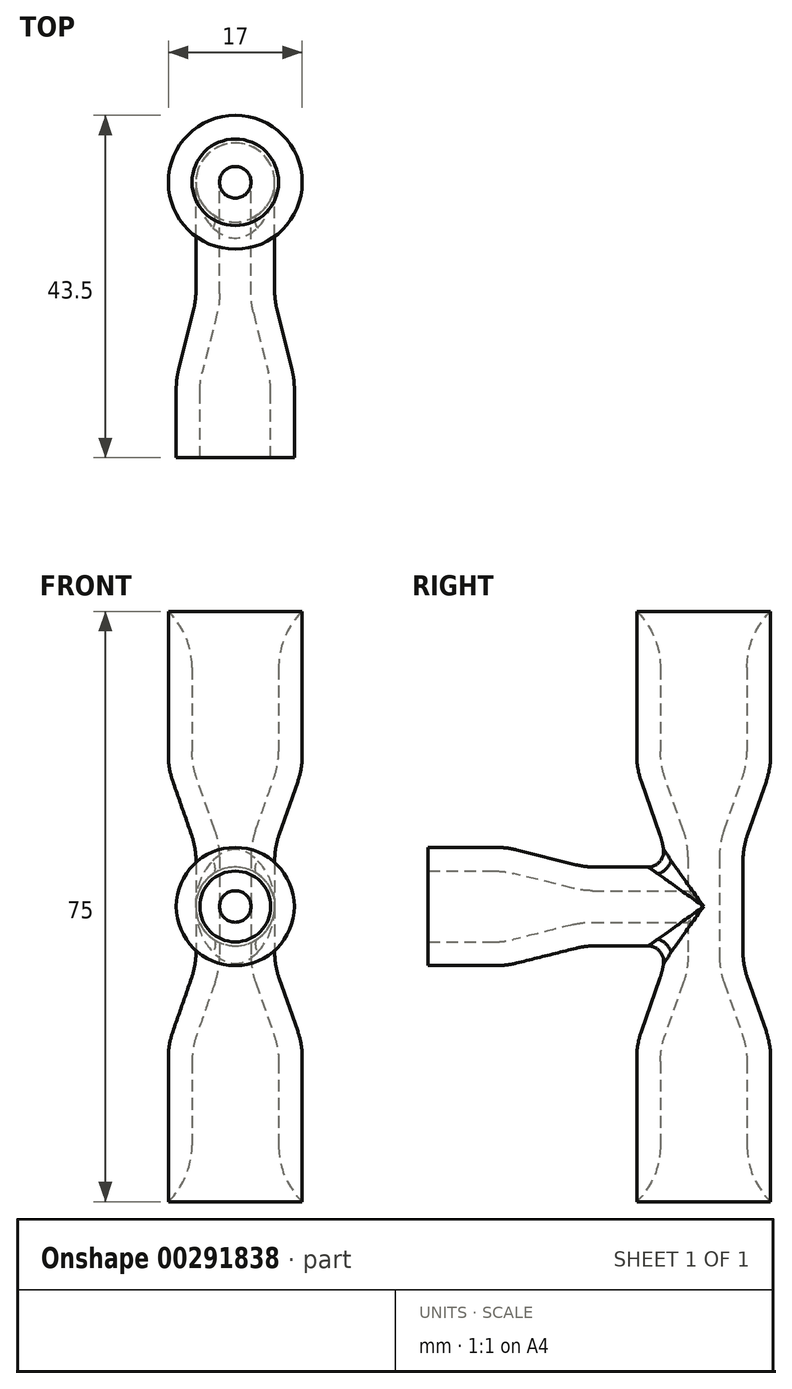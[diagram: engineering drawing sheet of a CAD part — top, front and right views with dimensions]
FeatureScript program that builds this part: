
annotation { "Feature Type Name" : "Feature", "Feature Type Description" : "" }
export const myFeature = defineFeature(function(context is Context, id is Id, definition is map)
    precondition{}
    {
        {
            var Q0;
            Q0=qCreatedBy(makeId("Top.planeOp"),FACE);
            var sketch = newSketch(context, id + "F0", { "sketchPlane" : qUnion([Q0])});
            skCircle(sketch, "E0", {"center": v(0, 0) * mm, "radius": 8.5 * mm});
            skSolve(sketch);
        }
        {
            var Q0;
            Q0=makeQuery(id+"F0.imprint","IMPRINT",FACE,{"disambiguationData":[TD([[makeQuery(id+"F0.imprint","IMPRINT",EDGE,{"derivedFrom":sQuery(id+"F0.wireOp",EDGE,"E0")}),1.0]])]});
            extrude(context, id + "F1", {"entities" : qUnion([Q0]), "depth" : 20 * mm});
        }
        {
            var Q0;
            Q0=makeQuery(id+"F1.opExtrude","CAP_FACE",FACE,{"disambiguationData":[OSD([sQuery(id+"F0.wireOp",EDGE,"E0")])],"isStart":false});
            cPlane(context, id + "F2", {"entities" : qUnion([Q0]), "cplaneType" : CPlaneType.OFFSET, "offset" : 10 * mm, "width" : 150 * mm, "height" : 150 * mm});
        }
        {
            var Q0;
            Q0=qCreatedBy(id+"F2.planeOp",FACE);
            var sketch = newSketch(context, id + "F3", { "sketchPlane" : qUnion([Q0])});
            skCircle(sketch, "E1.0", {"center": v(0, 0) * mm, "radius": 8.5 * mm, "construction": true});
            skCircle(sketch, "E2", {"center": v(0, 0) * mm, "radius": 5 * mm});
            skSolve(sketch);
        }
        {
            var Q1;
            Q1=makeQuery(id+"F1.opExtrude","CAP_FACE",FACE,{"disambiguationData":[OSD([sQuery(id+"F0.wireOp",EDGE,"E0")])],"isStart":false});
            var Q2;
            Q2=makeQuery(id+"F3.imprint","IMPRINT",FACE,{"disambiguationData":[TD([[makeQuery(id+"F3.imprint","IMPRINT",EDGE,{"derivedFrom":sQuery(id+"F3.wireOp",EDGE,"E2")}),1.0]])]});
            loft(context, id + "F4", {"operationType" : NewBodyOperationType.ADD, "sheetProfilesArray" : [{ "sheetProfileEntities" : qUnion([Q1]) }, { "sheetProfileEntities" : qUnion([Q2]) }]});
        }
        {
            var Q0;
            Q0=makeQuery(id+"F4.opLoft","CAP_FACE",FACE,{"disambiguationData":[OSD([makeQuery(id+"F3.imprint","IMPRINT",FACE,{"disambiguationData":[TD([[makeQuery(id+"F3.imprint","IMPRINT",EDGE,{"derivedFrom":sQuery(id+"F3.wireOp",EDGE,"E2")}),1.0]])]})])],"isStart":true});
            extrude(context, id + "F5", {"entities" : qUnion([Q0]), "operationType" : NewBodyOperationType.ADD, "depth" : 15 * mm});
        }
        {
            var Q0;
            Q0=makeQuery(id+"F5.opExtrude","CAP_FACE",FACE,{"disambiguationData":[OSD([makeQuery(id+"F3.imprint","IMPRINT",FACE,{"disambiguationData":[TD([[makeQuery(id+"F3.imprint","IMPRINT",EDGE,{"derivedFrom":sQuery(id+"F3.wireOp",EDGE,"E2")}),1.0]])]})])],"isStart":false});
            cPlane(context, id + "F6", {"entities" : qUnion([Q0]), "cplaneType" : CPlaneType.OFFSET, "offset" : 10 * mm, "width" : 150 * mm, "height" : 150 * mm});
        }
        {
            var Q0;
            Q0=qCreatedBy(id+"F6.planeOp",FACE);
            var sketch = newSketch(context, id + "F7", { "sketchPlane" : qUnion([Q0])});
            skCircle(sketch, "E3.0", {"center": v(0, 0) * mm, "radius": 8.5 * mm});
            skSolve(sketch);
        }
        {
            var Q1;
            Q1=makeQuery(id+"F7.imprint","IMPRINT",FACE,{"disambiguationData":[TD([[makeQuery(id+"F7.imprint","IMPRINT",EDGE,{"derivedFrom":sQuery(id+"F7.wireOp",EDGE,"E3.0")}),1.0]])]});
            var Q2;
            Q2=makeQuery(id+"F5.opExtrude","CAP_FACE",FACE,{"disambiguationData":[OSD([makeQuery(id+"F3.imprint","IMPRINT",FACE,{"disambiguationData":[TD([[makeQuery(id+"F3.imprint","IMPRINT",EDGE,{"derivedFrom":sQuery(id+"F3.wireOp",EDGE,"E2")}),1.0]])]})])],"isStart":false});
            loft(context, id + "F8", {"operationType" : NewBodyOperationType.ADD, "sheetProfilesArray" : [{ "sheetProfileEntities" : qUnion([Q1]) }, { "sheetProfileEntities" : qUnion([Q2]) }]});
        }
        {
            var Q0;
            Q0=makeQuery(id+"F8.opLoft","CAP_FACE",FACE,{"disambiguationData":[OSD([makeQuery(id+"F7.imprint","IMPRINT",FACE,{"disambiguationData":[TD([[makeQuery(id+"F7.imprint","IMPRINT",EDGE,{"derivedFrom":sQuery(id+"F7.wireOp",EDGE,"E3.0")}),1.0]])]})])],"isStart":true});
            extrude(context, id + "F9", {"entities" : qUnion([Q0]), "operationType" : NewBodyOperationType.ADD, "depth" : 20 * mm});
        }
        {
            var Q0;
            Q0=makeQuery(id+"F1.opExtrude","CAP_FACE",FACE,{"disambiguationData":[OSD([sQuery(id+"F0.wireOp",EDGE,"E0")])],"isStart":true});
            var Q1;
            Q1=makeQuery(id+"F9.opExtrude","CAP_FACE",FACE,{"disambiguationData":[OSD([makeQuery(id+"F7.imprint","IMPRINT",FACE,{"disambiguationData":[TD([[makeQuery(id+"F7.imprint","IMPRINT",EDGE,{"derivedFrom":sQuery(id+"F7.wireOp",EDGE,"E3.0")}),1.0]])]})])],"isStart":false});
            shell(context, id + "F10", {"entities" : qUnion([Q0, Q1]), "thickness" : 3 * mm});
        }
        {
            var Q0;
            Q0=qCreatedBy(makeId("Front.planeOp"),FACE);
            var sketch = newSketch(context, id + "F11", { "sketchPlane" : qUnion([Q0])});
            skLineSegment(sketch, "E4", {"start": v(5, 45) * mm, "end": v(5, 30) * mm});
            skLineSegment(sketch, "E5", {"start": v(-5, 30) * mm, "end": v(-5, 45) * mm});
            skLineSegment(sketch, "E6", {"start": v(5, 37.5) * mm, "end": v(-5, 37.5) * mm, "construction": true});
            skCircle(sketch, "E7", {"center": v(0, 37.5) * mm, "radius": 5 * mm});
            skSolve(sketch);
        }
        {
            var Q0;
            Q0=makeQuery(id+"F11.imprint","IMPRINT",FACE,{"disambiguationData":[TD([[makeQuery(id+"F11.imprint","IMPRINT",EDGE,{"derivedFrom":sQuery(id+"F11.wireOp",EDGE,"E7")}),1.0]])]});
            extrude(context, id + "F12", {"entities" : qUnion([Q0]), "depth" : 15 * mm});
        }
        {
            var Q0;
            Q0=makeQuery(id+"F12.opExtrude","CAP_FACE",FACE,{"disambiguationData":[OSD([sQuery(id+"F11.wireOp",EDGE,"E7")])],"isStart":false});
            cPlane(context, id + "F13", {"entities" : qUnion([Q0]), "cplaneType" : CPlaneType.OFFSET, "offset" : 10 * mm, "width" : 150 * mm, "height" : 150 * mm});
        }
        {
            var Q0;
            Q0=qCreatedBy(id+"F13.planeOp",FACE);
            var sketch = newSketch(context, id + "F14", { "sketchPlane" : qUnion([Q0])});
            skCircle(sketch, "E8.0", {"center": v(0, 37.5) * mm, "radius": 5 * mm, "construction": true});
            skCircle(sketch, "E9", {"center": v(0, 37.5) * mm, "radius": 7.5 * mm});
            skSolve(sketch);
        }
        {
            var Q1;
            Q1=makeQuery(id+"F12.opExtrude","CAP_FACE",FACE,{"disambiguationData":[OSD([sQuery(id+"F11.wireOp",EDGE,"E7")])],"isStart":false});
            var Q2;
            Q2=makeQuery(id+"F14.imprint","IMPRINT",FACE,{"disambiguationData":[TD([[makeQuery(id+"F14.imprint","IMPRINT",EDGE,{"derivedFrom":sQuery(id+"F14.wireOp",EDGE,"E9")}),1.0]])]});
            loft(context, id + "F15", {"operationType" : NewBodyOperationType.ADD, "sheetProfilesArray" : [{ "sheetProfileEntities" : qUnion([Q1]) }, { "sheetProfileEntities" : qUnion([Q2]) }]});
        }
        {
            var Q0;
            Q0=makeQuery(id+"F15.opLoft","CAP_FACE",FACE,{"disambiguationData":[OSD([makeQuery(id+"F14.imprint","IMPRINT",FACE,{"disambiguationData":[TD([[makeQuery(id+"F14.imprint","IMPRINT",EDGE,{"derivedFrom":sQuery(id+"F14.wireOp",EDGE,"E9")}),1.0]])]})])],"isStart":true});
            extrude(context, id + "F16", {"entities" : qUnion([Q0]), "operationType" : NewBodyOperationType.ADD, "depth" : 10 * mm});
        }
        {
            var Q0;
            Q0=makeQuery(id+"F16.opExtrude","CAP_FACE",FACE,{"disambiguationData":[OSD([makeQuery(id+"F14.imprint","IMPRINT",FACE,{"disambiguationData":[TD([[makeQuery(id+"F14.imprint","IMPRINT",EDGE,{"derivedFrom":sQuery(id+"F14.wireOp",EDGE,"E9")}),1.0]])]})])],"isStart":false});
            var Q1;
            Q1=makeQuery(id+"F12.opExtrude","CAP_FACE",FACE,{"disambiguationData":[OSD([sQuery(id+"F11.wireOp",EDGE,"E7")])],"isStart":true});
            shell(context, id + "F17", {"entities" : qUnion([Q0, Q1]), "thickness" : 3 * mm});
        }
        {
            var Q0;
            Q0=makeQuery(id+"F12.opExtrude","SWEPT_BODY",BODY,{"disambiguationData":[OSD([sQuery(id+"F11.wireOp",EDGE,"E7")])]});
            var Q1;
            Q1=makeQuery(id+"F1.opExtrude","SWEPT_BODY",BODY,{"disambiguationData":[OSD([sQuery(id+"F0.wireOp",EDGE,"E0")])]});
            booleanBodies(context, id + "F18", {"operationType" : BooleanOperationType.UNION, "tools" : qUnion([Q0, Q1])});
        }
        {
            var Q0;
            Q0=makeQuery(id+"F9.opExtrude","CAP_FACE",FACE,{"disambiguationData":[OSD([makeQuery(id+"F7.imprint","IMPRINT",FACE,{"disambiguationData":[TD([[makeQuery(id+"F7.imprint","IMPRINT",EDGE,{"derivedFrom":sQuery(id+"F7.wireOp",EDGE,"E3.0")}),1.0]])]})])],"isStart":false});
            var sketch = newSketch(context, id + "F19", { "sketchPlane" : qUnion([Q0])});
            skCircle(sketch, "E10.0", {"center": v(0, 0) * mm, "radius": 2 * mm});
            skSolve(sketch);
        }
        {
            var Q0;
            Q0=makeQuery(id+"F19.imprint","IMPRINT",FACE,{"disambiguationData":[TD([[makeQuery(id+"F19.imprint","IMPRINT",EDGE,{"derivedFrom":sQuery(id+"F19.wireOp",EDGE,"E10.0")}),1.0]])]});
            extrude(context, id + "F20", {"entities" : qUnion([Q0]), "operationType" : NewBodyOperationType.REMOVE, "oppositeDirection" : true, "depth" : 100 * mm});
        }
        {
            var Q0;
            Q0=makeQuery(id+"F16.opExtrude","CAP_FACE",FACE,{"disambiguationData":[OSD([makeQuery(id+"F14.imprint","IMPRINT",FACE,{"disambiguationData":[TD([[makeQuery(id+"F14.imprint","IMPRINT",EDGE,{"derivedFrom":sQuery(id+"F14.wireOp",EDGE,"E9")}),1.0]])]})])],"isStart":false});
            var sketch = newSketch(context, id + "F21", { "sketchPlane" : qUnion([Q0])});
            skCircle(sketch, "E11.0", {"center": v(0, 37.5) * mm, "radius": 2 * mm});
            skSolve(sketch);
        }
        {
            var Q0;
            Q0=makeQuery(id+"F21.imprint","IMPRINT",FACE,{"disambiguationData":[TD([[makeQuery(id+"F21.imprint","IMPRINT",EDGE,{"derivedFrom":sQuery(id+"F21.wireOp",EDGE,"E11.0")}),1.0]])]});
            extrude(context, id + "F22", {"entities" : qUnion([Q0]), "operationType" : NewBodyOperationType.REMOVE, "oppositeDirection" : true, "depth" : 35 * mm});
        }
        {
            var Q0;
            {var subQ0=sQuery(id+"F0.wireOp",EDGE,"E0");Q0=makeQuery(id+"F10.opShell","OFFSET_EDGE",EDGE,{"disambiguationData":[OSD([subQ0]),TDD([makeQuery(id+"F4.boolean.opBoolean","MERGE",EDGE,{"derivedFrom":[makeQuery(id+"F1.opExtrude","CAP_EDGE",EDGE,{"disambiguationData":[OSD([subQ0])],"isStart":false}),makeQuery(id+"F4.opLoft","MID_CAP_EDGE",EDGE,{"disambiguationData":[OSD([subQ0])],"capPos":0.0})]})])]});}
            var Q1;
            Q1=makeQuery(id+"F10.opShell","OFFSET_EDGE",EDGE,{"disambiguationData":[OSD([sQuery(id+"F0.wireOp",EDGE,"E0"),sQuery(id+"F3.wireOp",EDGE,"E2")])]});
            var Q2;
            Q2=makeQuery(id+"F10.opShell","OFFSET_EDGE",EDGE,{"disambiguationData":[OSD([sQuery(id+"F0.wireOp",EDGE,"E0"),sQuery(id+"F3.wireOp",EDGE,"E2"),sQuery(id+"F7.wireOp",EDGE,"E3.0")])]});
            var Q3;
            {var subQ0=sQuery(id+"F7.wireOp",EDGE,"E3.0");Q3=makeQuery(id+"F10.opShell","OFFSET_EDGE",EDGE,{"disambiguationData":[OSD([subQ0]),TDD([makeQuery(id+"F9.boolean.opBoolean","MERGE",EDGE,{"derivedFrom":[makeQuery(id+"F8.opLoft","MID_CAP_EDGE",EDGE,{"disambiguationData":[OSD([subQ0])],"capPos":0.0}),makeQuery(id+"F9.opExtrude","CAP_EDGE",EDGE,{"disambiguationData":[OSD([subQ0])],"isStart":true})]})])]});}
            var Q4;
            {var subQ0=sQuery(id+"F7.wireOp",EDGE,"E3.0");Q4=makeQuery(id+"F9.boolean.opBoolean","MERGE",EDGE,{"derivedFrom":[makeQuery(id+"F8.opLoft","MID_CAP_EDGE",EDGE,{"disambiguationData":[OSD([subQ0])],"capPos":0.0}),makeQuery(id+"F9.opExtrude","CAP_EDGE",EDGE,{"disambiguationData":[OSD([subQ0])],"isStart":true})]});}
            var Q5;
            {var subQ0=sQuery(id+"F3.wireOp",EDGE,"E2");var subQ1=sQuery(id+"F0.wireOp",EDGE,"E0");Q5=makeQuery(id+"F8.boolean.opBoolean","MERGE",EDGE,{"derivedFrom":[makeQuery(id+"F5.opExtrude","CAP_EDGE",EDGE,{"disambiguationData":[OSD([subQ1,subQ0])],"isStart":false}),makeQuery(id+"F8.opLoft","MID_CAP_EDGE",EDGE,{"disambiguationData":[OSD([subQ1,subQ0,sQuery(id+"F7.wireOp",EDGE,"E3.0")])],"capPos":1.0})]});}
            var Q6;
            {var subQ0=sQuery(id+"F3.wireOp",EDGE,"E2");var subQ1=sQuery(id+"F0.wireOp",EDGE,"E0");Q6=makeQuery(id+"F5.boolean.opBoolean","MERGE",EDGE,{"derivedFrom":[makeQuery(id+"F4.opLoft","MID_CAP_EDGE",EDGE,{"disambiguationData":[OSD([subQ1,subQ0])],"capPos":1.0}),makeQuery(id+"F5.opExtrude","CAP_EDGE",EDGE,{"disambiguationData":[OSD([subQ1,subQ0])],"isStart":true})]});}
            var Q7;
            {var subQ0=sQuery(id+"F0.wireOp",EDGE,"E0");Q7=makeQuery(id+"F4.boolean.opBoolean","MERGE",EDGE,{"derivedFrom":[makeQuery(id+"F1.opExtrude","CAP_EDGE",EDGE,{"disambiguationData":[OSD([subQ0])],"isStart":false}),makeQuery(id+"F4.opLoft","MID_CAP_EDGE",EDGE,{"disambiguationData":[OSD([subQ0])],"capPos":0.0})]});}
            var Q8;
            {var subQ0=sQuery(id+"F11.wireOp",EDGE,"E7");Q8=makeQuery(id+"F15.boolean.opBoolean","MERGE",EDGE,{"derivedFrom":[makeQuery(id+"F12.opExtrude","CAP_EDGE",EDGE,{"disambiguationData":[OSD([subQ0])],"isStart":false}),makeQuery(id+"F15.opLoft","MID_CAP_EDGE",EDGE,{"disambiguationData":[OSD([subQ0])],"capPos":0.0})]});}
            var Q9;
            {var subQ0=sQuery(id+"F14.wireOp",EDGE,"E9");var subQ1=sQuery(id+"F11.wireOp",EDGE,"E7");Q9=makeQuery(id+"F16.boolean.opBoolean","MERGE",EDGE,{"derivedFrom":[makeQuery(id+"F15.opLoft","MID_CAP_EDGE",EDGE,{"disambiguationData":[OSD([subQ1,subQ0])],"capPos":1.0}),makeQuery(id+"F16.opExtrude","CAP_EDGE",EDGE,{"disambiguationData":[OSD([subQ1,subQ0])],"isStart":true})]});}
            var Q10;
            {var subQ0=sQuery(id+"F11.wireOp",EDGE,"E7");Q10=makeQuery(id+"F17.opShell","OFFSET_EDGE",EDGE,{"disambiguationData":[OSD([subQ0]),TDD([makeQuery(id+"F15.boolean.opBoolean","MERGE",EDGE,{"derivedFrom":[makeQuery(id+"F12.opExtrude","CAP_EDGE",EDGE,{"disambiguationData":[OSD([subQ0])],"isStart":false}),makeQuery(id+"F15.opLoft","MID_CAP_EDGE",EDGE,{"disambiguationData":[OSD([subQ0])],"capPos":0.0})]})])]});}
            var Q11;
            {var subQ0=sQuery(id+"F14.wireOp",EDGE,"E9");var subQ1=sQuery(id+"F11.wireOp",EDGE,"E7");Q11=makeQuery(id+"F17.opShell","OFFSET_EDGE",EDGE,{"disambiguationData":[OSD([subQ1,subQ0]),TDD([makeQuery(id+"F16.boolean.opBoolean","MERGE",EDGE,{"derivedFrom":[makeQuery(id+"F15.opLoft","MID_CAP_EDGE",EDGE,{"disambiguationData":[OSD([subQ1,subQ0])],"capPos":1.0}),makeQuery(id+"F16.opExtrude","CAP_EDGE",EDGE,{"disambiguationData":[OSD([subQ1,subQ0])],"isStart":true})]})])]});}
            fillet(context, id + "F23", {"entities" : qUnion([Q0, Q1, Q2, Q3, Q4, Q5, Q6, Q7, Q8, Q9, Q10, Q11]), "radius" : 10 * mm, "tangentPropagation" : true, "allowEdgeOverflow" : false});
        }
        {
            var Q0;
            Q0=makeQuery(id+"F18.opBoolean","INTERSECT",EDGE,{"disambiguationData":[OD(0.0)],"derivedFrom":[makeQuery(id+"F5.opExtrude","SWEPT_FACE",FACE,{"disambiguationData":[OSD([sQuery(id+"F0.wireOp",EDGE,"E0"),sQuery(id+"F3.wireOp",EDGE,"E2")])]}),makeQuery(id+"F12.opExtrude","SWEPT_FACE",FACE,{"disambiguationData":[OSD([sQuery(id+"F11.wireOp",EDGE,"E7")])]})]});
            var Q1;
            Q1=makeQuery(id+"F18.opBoolean","INTERSECT",EDGE,{"disambiguationData":[OD(1.0)],"derivedFrom":[makeQuery(id+"F5.opExtrude","SWEPT_FACE",FACE,{"disambiguationData":[OSD([sQuery(id+"F0.wireOp",EDGE,"E0"),sQuery(id+"F3.wireOp",EDGE,"E2")])]}),makeQuery(id+"F12.opExtrude","SWEPT_FACE",FACE,{"disambiguationData":[OSD([sQuery(id+"F11.wireOp",EDGE,"E7")])]})]});
            fillet(context, id + "F24", {"entities" : qUnion([Q0, Q1]), "radius" : 2 * mm, "tangentPropagation" : true, "allowEdgeOverflow" : false});
        }
    });
